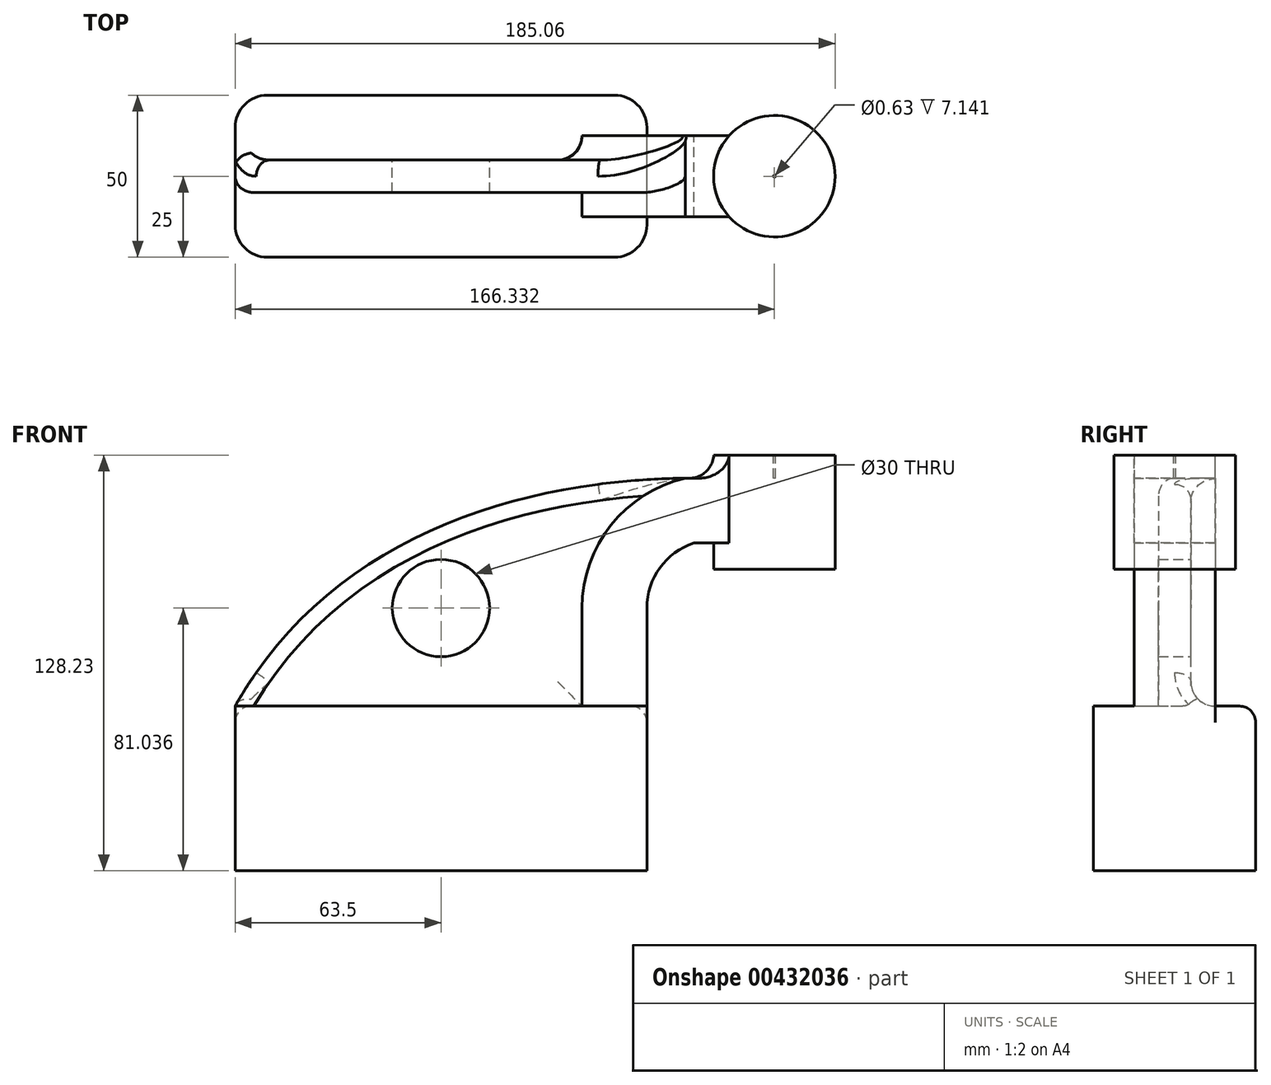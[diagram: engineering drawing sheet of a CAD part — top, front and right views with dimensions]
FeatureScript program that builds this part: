
annotation { "Feature Type Name" : "Feature", "Feature Type Description" : "" }
export const myFeature = defineFeature(function(context is Context, id is Id, definition is map)
    precondition{}
    {
        {
            var Q0;
            Q0=qCreatedBy(makeId("Front.planeOp"),FACE);
            var sketch = newSketch(context, id + "F0", { "sketchPlane" : qUnion([Q0])});
            skLineSegment(sketch, "E0.bottom", {"start": v(-63.5, 25.4) * mm, "end": v(63.5, 25.4) * mm});
            skLineSegment(sketch, "E0.top", {"start": v(-63.5, -25.4) * mm, "end": v(63.5, -25.4) * mm});
            skLineSegment(sketch, "E0.left", {"start": v(-63.5, 25.4) * mm, "end": v(-63.5, -25.4) * mm});
            skLineSegment(sketch, "E0.right", {"start": v(63.5, 25.4) * mm, "end": v(63.5, -25.4) * mm});
            skPoint(sketch, "E0.middle", {"position": v(0, 0) * mm});
            skLineSegment(sketch, "E1.bottom", {"start": v(121.56, 67.6) * mm, "end": v(84.1, 67.6) * mm});
            skLineSegment(sketch, "E1.top", {"start": v(121.56, 102.83) * mm, "end": v(84.1, 102.83) * mm});
            skLineSegment(sketch, "E1.left", {"start": v(121.56, 67.6) * mm, "end": v(121.56, 102.83) * mm});
            skLineSegment(sketch, "E1.right", {"start": v(84.1, 67.6) * mm, "end": v(84.1, 102.83) * mm});
            skPoint(sketch, "E1.middle", {"position": v(102.83, 85.22) * mm});
            skLineSegment(sketch, "E2", {"start": v(63.5, 25.4) * mm, "end": v(63.5, 55.7) * mm});
            skArc(sketch, "E3", {"start": v(78, 75.7) * mm, "mid": v(67.5, 68.04) * mm, "end": v(63.5, 55.7) * mm});
            skLineSegment(sketch, "E4", {"start": v(78, 75.7) * mm, "end": v(102.83, 75.7) * mm});
            skLineSegment(sketch, "E5.0", {"start": v(75.34, 95.7) * mm, "end": v(103.15, 95.7) * mm});
            skArc(sketch, "E5.1", {"start": v(75.34, 95.7) * mm, "mid": v(52.43, 81.25) * mm, "end": v(43.5, 55.7) * mm});
            skLineSegment(sketch, "E5.2", {"start": v(43.5, 25.4) * mm, "end": v(43.5, 55.7) * mm});
            skLineSegment(sketch, "E6", {"start": v(102.83, 75.7) * mm, "end": v(102.83, 85.22) * mm});
            skLineSegment(sketch, "E7", {"start": v(102.83, 85.22) * mm, "end": v(103.15, 95.7) * mm});
            skLineSegment(sketch, "E8", {"start": v(103.15, 95.7) * mm, "end": v(103.15, 102.83) * mm});
            skPoint(sketch, "E8.endSnap0", {"position": v(102.83, 102.83) * mm});
            skFitSpline(sketch, "E9", {"points": [v(-63.5, 25.4) * mm, v(75.34, 95.7) * mm], "startDerivative": vector(85.76, 151.84) * mm, "endDerivative": vector(163.18, 1.9) * mm});
            skLineSegment(sketch, "E10", {"start": v(102.83, 75.7) * mm, "end": v(102.83, 67.6) * mm});
            skCircle(sketch, "E11", {"center": v(0, 55.64) * mm, "radius": 15 * mm});
            skSolve(sketch);
        }
        {
            var Q0;
            Q0=makeQuery(id+"F0.imprint","IMPRINT",FACE,{"disambiguationData":[TD([[makeQuery(id+"F0.imprint","IMPRINT",EDGE,{"derivedFrom":sQuery(id+"F0.wireOp",EDGE,"E0.top")}),1.0]])]});
            extrude(context, id + "F1", {"entities" : qUnion([Q0]), "endBound" : BoundingType.SYMMETRIC, "depth" : 50 * mm});
        }
        {
            var Q0;
            {var subQ1=sQuery(id+"F0.wireOp",EDGE,"E2");Q0=makeQuery(id+"F0.imprint","IMPRINT",FACE,{"disambiguationData":[TD([[makeQuery(id+"F0.imprint","IMPRINT",EDGE,{"derivedFrom":subQ1}),1.0]])]});}
            var Q1;
            {var subQ4=sQuery(id+"F0.wireOp",EDGE,"E6");Q1=makeQuery(id+"F0.imprint","IMPRINT",FACE,{"disambiguationData":[TD([[makeQuery(id+"F0.imprint","IMPRINT",EDGE,{"derivedFrom":subQ4}),1.0]])]});}
            extrude(context, id + "F2", {"entities" : qUnion([Q0, Q1]), "operationType" : NewBodyOperationType.ADD, "endBound" : BoundingType.SYMMETRIC, "depth" : 25 * mm});
        }
        {
            var Q0;
            Q0=makeQuery(id+"F0.imprint","IMPRINT",FACE,{"disambiguationData":[TD([[makeQuery(id+"F0.imprint","IMPRINT",EDGE,{"derivedFrom":sQuery(id+"F0.wireOp",EDGE,"E5.1")}),-1.0]])]});
            extrude(context, id + "F3", {"entities" : qUnion([Q0]), "operationType" : NewBodyOperationType.ADD, "endBound" : BoundingType.SYMMETRIC, "depth" : 10 * mm});
        }
        {
            var Q0;
            {var subQ0=sQuery(id+"F0.wireOp",EDGE,"E1.left");Q0=makeQuery(id+"F0.imprint","IMPRINT",FACE,{"disambiguationData":[TD([[makeQuery(id+"F0.imprint","IMPRINT",EDGE,{"derivedFrom":subQ0}),1.0]])]});}
            var Q1;
            Q1=sQuery(id+"F0.wireOp",EDGE,"E10");
            revolve(context, id + "F4", {"entities" : qUnion([Q0]), "axis" : qUnion([Q1]), "revolveType" : RevolveType.FULL});
        }
        {
            var Q0;
            Q0=makeQuery(id+"F1.opExtrude","CAP_EDGE",EDGE,{"disambiguationData":[OSD([sQuery(id+"F0.wireOp",EDGE,"E0.right")])],"isStart":false});
            var Q1;
            Q1=makeQuery(id+"F1.opExtrude","CAP_EDGE",EDGE,{"disambiguationData":[OSD([sQuery(id+"F0.wireOp",EDGE,"E0.left")])],"isStart":false});
            var Q2;
            Q2=makeQuery(id+"F1.opExtrude","CAP_EDGE",EDGE,{"disambiguationData":[OSD([sQuery(id+"F0.wireOp",EDGE,"E0.left")])],"isStart":true});
            var Q3;
            Q3=makeQuery(id+"F1.opExtrude","CAP_EDGE",EDGE,{"disambiguationData":[OSD([sQuery(id+"F0.wireOp",EDGE,"E0.right")])],"isStart":true});
            fillet(context, id + "F5", {"entities" : qUnion([Q0, Q1, Q2, Q3]), "radius" : 10 * mm, "tangentPropagation" : true, "allowEdgeOverflow" : false});
        }
        {
            var Q0;
            Q0=makeQuery(id+"F1.opExtrude","SWEPT_BODY",BODY,{"disambiguationData":[OSD([sQuery(id+"F0.wireOp",EDGE,"E0.bottom"),sQuery(id+"F0.wireOp",EDGE,"E0.top"),sQuery(id+"F0.wireOp",EDGE,"E0.left"),sQuery(id+"F0.wireOp",EDGE,"E0.right")])]});
            var Q1;
            Q1=makeQuery(id+"F4.opRevolve","SWEPT_BODY",BODY,{"disambiguationData":[OSD([sQuery(id+"F0.wireOp",EDGE,"E1.bottom"),sQuery(id+"F0.wireOp",EDGE,"E1.top"),sQuery(id+"F0.wireOp",EDGE,"E1.left"),sQuery(id+"F0.wireOp",EDGE,"E6"),sQuery(id+"F0.wireOp",EDGE,"E7"),sQuery(id+"F0.wireOp",EDGE,"E8"),sQuery(id+"F0.wireOp",EDGE,"E10")])]});
            booleanBodies(context, id + "F6", {"operationType" : BooleanOperationType.UNION, "tools" : qUnion([Q0, Q1])});
        }
        {
            var Q0;
            Q0=makeQuery(id+"F3.opExtrude","CAP_EDGE",EDGE,{"disambiguationData":[OSD([sQuery(id+"F0.wireOp",EDGE,"E0.bottom")])],"isStart":false});
            var Q1;
            Q1=makeQuery(id+"F3.opExtrude","CAP_EDGE",EDGE,{"disambiguationData":[OSD([sQuery(id+"F0.wireOp",EDGE,"E0.bottom")])],"isStart":true});
            var Q2;
            Q2=makeQuery(id+"F6.opBoolean","INTERSECT",EDGE,{"derivedFrom":[makeQuery(id+"F2.opExtrude","SWEPT_FACE",FACE,{"disambiguationData":[OSD([sQuery(id+"F0.wireOp",EDGE,"E5.0")])]}),makeQuery(id+"F4.opRevolve","SWEPT_FACE",FACE,{"disambiguationData":[OSD([sQuery(id+"F0.wireOp",EDGE,"E1.left")])]})]});
            var Q3;
            Q3=makeQuery(id+"F3.opExtrude","CAP_EDGE",EDGE,{"disambiguationData":[OSD([sQuery(id+"F0.wireOp",EDGE,"E5.2")])],"isStart":true});
            var Q4;
            Q4=makeQuery(id+"F3.opExtrude","CAP_EDGE",EDGE,{"disambiguationData":[OSD([sQuery(id+"F0.wireOp",EDGE,"E5.1")])],"isStart":false});
            fillet(context, id + "F7", {"entities" : qUnion([Q0, Q1, Q2, Q3, Q4]), "radius" : 7.5 * mm, "tangentPropagation" : true, "allowEdgeOverflow" : false});
        }
        {
            var Q0;
            Q0=makeQuery(id+"F3.opExtrude","CAP_EDGE",EDGE,{"disambiguationData":[OSD([sQuery(id+"F0.wireOp",EDGE,"E9")])],"isStart":false});
            var Q1;
            Q1=makeQuery(id+"F2.opExtrude","CAP_EDGE",EDGE,{"disambiguationData":[OSD([sQuery(id+"F0.wireOp",EDGE,"E0.bottom")])],"isStart":false});
            var Q2;
            Q2=makeQuery(id+"F3.opExtrude","CAP_EDGE",EDGE,{"disambiguationData":[OSD([sQuery(id+"F0.wireOp",EDGE,"E9")])],"isStart":true});
            fillet(context, id + "F8", {"entities" : qUnion([Q0, Q1, Q2]), "radius" : 5 * mm, "tangentPropagation" : true, "allowEdgeOverflow" : false});
        }
    });
